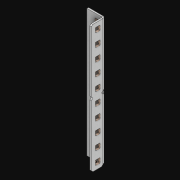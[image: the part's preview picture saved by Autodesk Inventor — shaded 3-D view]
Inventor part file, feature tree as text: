
AUTODESK INVENTOR PART (.ipt)
format: ipt  version: 2021 (Build 250183000, 183)  size: 1,110,528 bytes
history: native  units: in
note: dims shown in document units (in); Inventor stores cm internally (conversion verified against a paired STEP export)
features: extrude x22, other x20, sketch x4, pattern_linear x2, sheet_metal_op x1
ambient origin geometry x8: Origin, YZ Plane, XZ Plane, XY Plane, X Axis, Y Axis, Z Axis, Center Point
bodies: Solid1 (feature_tree)
feature tree (49):
  pattern_linear  "Rectangular Pattern1"  Spacing1=0.5in  [1 undecoded]
  pattern_linear  "Rectangular Pattern3"  Count1=10  [1 undecoded]
  extrude  "Extrusion1"  Depth=0.5in
  extrude  "Extrusion2"  Depth=0.5in
  sketch  "Sketch1"  dims[d0=0.182in]
  other  "Srf1"
  sketch  "Sketch3"  dims[d1=0.063in d2=0.0in]
  other  "Srf3"
  other  "Srf4"
  other  "Srf5"
  other  "Srf6"
  other  "Srf7"
  other  "Srf8"
  other  "Srf9"
  other  "Srf10"
  other  "Srf11"
  other  "Srf12"
  other  "Srf142"
  other  "Srf143"
  other  "Srf144"
  other  "Srf145"
  other  "Srf146"
  other  "Srf147"
  other  "Srf148"
  other  "Srf149"
  other  "Srf150"
  sketch  "Sketch4"  dims[d6=0.182in]
  sketch  "Sketch5"  dims[d7=0.063in d8=0.0in d11=0.5in d12=0.3937in d14=0.5in d18=3.937in d20=0.5in d21=12.5in d22=0.0in d23=0.841in d24=0.0in]
  sheet_metal_op  "Fold1"
  extrude  "ExtrusionSrf1"  TaperAngle=0.0deg  [1 undecoded]
  extrude  "ExtrusionSrf3"  Depth=0.5in TaperAngle=0.0deg
  extrude  "ExtrusionSrf4"  [1 undecoded]
  extrude  "ExtrusionSrf5"  [1 undecoded]
  extrude  "ExtrusionSrf6"  [1 undecoded]
  extrude  "ExtrusionSrf7"  [1 undecoded]
  extrude  "ExtrusionSrf8"  [1 undecoded]
  extrude  "ExtrusionSrf9"  [1 undecoded]
  extrude  "ExtrusionSrf10"  [1 undecoded]
  extrude  "ExtrusionSrf11"  [1 undecoded]
  extrude  "ExtrusionSrf12"  [1 undecoded]
  extrude  "ExtrusionSrf142"  [1 undecoded]
  extrude  "ExtrusionSrf143"  [1 undecoded]
  extrude  "ExtrusionSrf144"  [1 undecoded]
  extrude  "ExtrusionSrf145"  [1 undecoded]
  extrude  "ExtrusionSrf146"  [1 undecoded]
  extrude  "ExtrusionSrf147"  [1 undecoded]
  extrude  "ExtrusionSrf148"  [1 undecoded]
  extrude  "ExtrusionSrf149"  [1 undecoded]
  extrude  "ExtrusionSrf150"  [1 undecoded]
note: 21 required parameter values undecoded (feature->parameter linkage not recoverable at this tier; creation-order binding heuristic only, values carry confidence <= 0.55)
